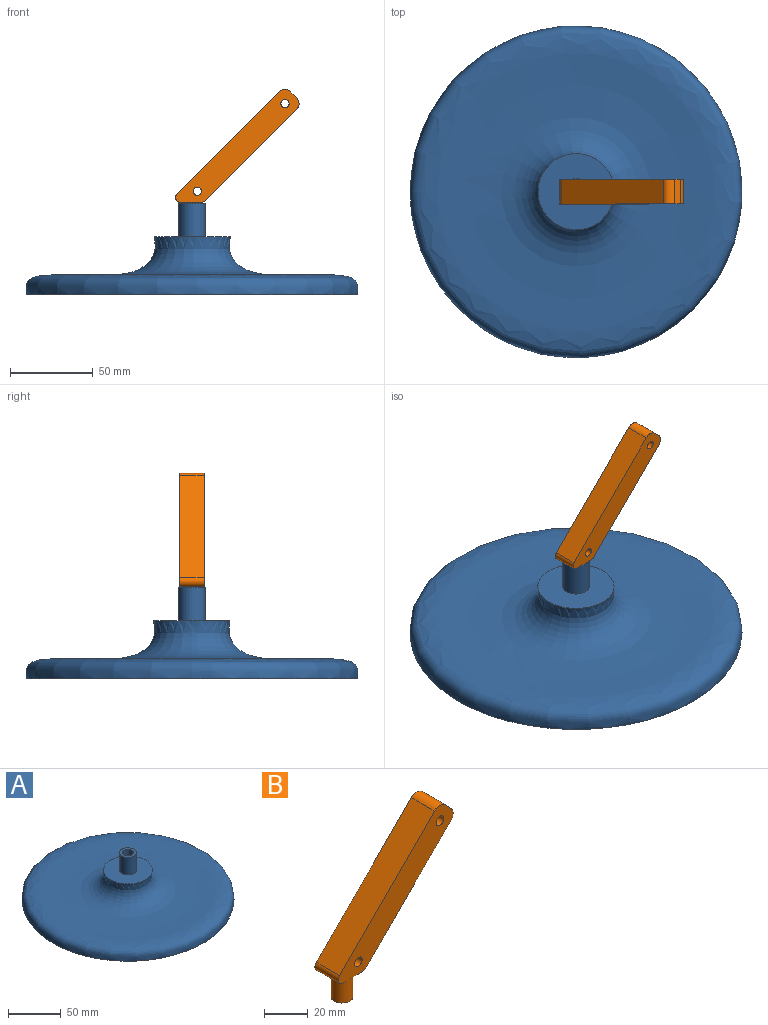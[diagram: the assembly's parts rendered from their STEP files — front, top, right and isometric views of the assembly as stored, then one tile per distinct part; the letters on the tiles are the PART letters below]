
ASSEMBLY  parts=2 mates=1
PART A: 7 faces, bbox 200.5x200.5x55 mm
  f0: plane 200x200mm, normal (0,0,-1), area 31415.9mm2, adj f1
  f1: revolved ~200.48x200.48mm, area 37173.4mm2, adj f0,f2
  f2: plane 46x46mm, normal (0,0,1), area 1460.8mm2, adj f1,f3
  f3: cylinder r=8mm len=20mm, axis (0,0,-1), area 1005.3mm2, adj f2,f4
  f4: plane 16x16mm, normal (0,0,1), area 122.5mm2, adj f3,f5
  f5: cylinder r=5mm len=15mm, axis (0,0,1), area 471.2mm2, adj f4,f6
  f6: plane 10x10mm, normal (0,0,1), area 78.5mm2, adj f5
PART B: 16 faces, bbox 74.5x15x83.1 mm
  f0: cylinder r=3mm len=15mm, axis (0,1,0), area 106mm2, adj f1,f8,f9,f10
  f1: plane 15x11.9mm, normal (0,0,-1), area 100.1mm2, adj f0,f9,f10,f11,f13,f15
  f2: plane 54.59x54.59mm, normal (0.71,0,-0.71), area 1158.1mm2, adj f3,f9,f10,f13,f14,f15
  f3: cylinder r=5mm len=15mm, axis (0,1,0), area 117.8mm2, adj f2,f4,f9,f10
  f4: plane 15x3.54mm, normal (0.71,0,0.71), area 75mm2, adj f3,f5,f9,f10
  f5: cylinder r=5mm len=15mm, axis (0,1,0), area 117.8mm2, adj f4,f8,f9,f10
  f6: cylinder r=2.5mm len=15mm, axis (0,1,0), area 235.6mm2, adj f9,f10
  f7: cylinder r=2.5mm len=15mm, axis (0,1,0), area 235.6mm2, adj f9,f10
  f8: plane 61.54x61.54mm, normal (-0.71,0,0.71), area 1305.5mm2, adj f0,f5,f9,f10
  f9: plane 74.49x68.13mm, normal (0,-1,0), area 1315mm2, adj f0,f1,f2,f3,f4,f5,f6,f7
  f10: plane 74.49x68.13mm, normal (0,1,0), area 1315mm2, adj f0,f1,f2,f3,f4,f5,f6,f7
  f11: cylinder r=5mm len=15mm, axis (0,0,1), area 471.2mm2, adj f1,f12,f14
  f12: plane 10x10mm, normal (0,0,-1), area 78.5mm2, adj f11
  f13: cylinder r=5mm len=6.58mm, axis (0,1,0), area 25.8mm2, adj f1,f2,f10,f14
  f14: bspline ~3.64x2.58mm, area 7.1mm2, adj f2,f11,f13,f15
  f15: cylinder r=5mm len=6.58mm, axis (0,1,0), area 25.8mm2, adj f1,f2,f9,f14
PLACE A rot(axis=(0,0,-1),0deg) t=(-45.69,-10.55,0.88)mm
PLACE B t=(-50.95,-3.05,43.74)mm
MATE cylindrical B.f11 <-> A.f5  axis (0,0,1) through (-45.69,-10.55,51.24)mm
